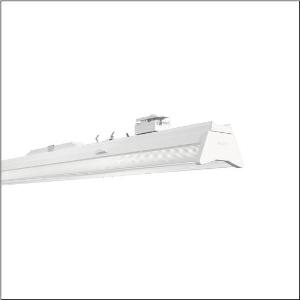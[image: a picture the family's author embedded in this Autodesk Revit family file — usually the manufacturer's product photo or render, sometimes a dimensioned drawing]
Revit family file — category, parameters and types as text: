
# Revit family: licross_r__11_performance_ho_51tm16dn4fxm_a8d0
name_source: partatom
category: Lighting Fixtures
units: mm (PartAtom-declared; Revit-internal decimal feet)

## family parameters
Cut with Voids When Loaded = No
Host = Face
Light Source = No
Part Type = Normal
Room Calculation Point = No
Round Connector Dimension = Use Diameter
Shared = No

## types (1)
- --- (1 x LED, 15460 lm, 87.3 W, 4000K)
    Apparent Load = 87 VA
    CIE Flux Codes = 63 87 95 78 100
    Color Rendering = 80
    Color Temperature = 4000K
    Default Elevation = 1800 mm
    Description = Licross® 11 Performance HO, luminaire insert, of sheet steel, galvanised, coil coated, white, length: 1.500mm, width: 120mm, height: 123mm, LED rated luminous flux: 15.460lm, light colour: 840, control gear: DALI 2, with plug, 5-pole, with phase selection, mains connection: 220..240V, AC, 50/60Hz, rated input power: 87W, halogen-free wiring, primary light control with lens, of plastic, primary optical cover: cover, of PMMA, light emission: direct/indirect distribution, primary light characteristic: symmetric, protection rating (complete): IP40, insulation class (complete): insulation class I (protective earthing), certification: CE, ENEC, VDE, UKCA, protection symbol: D if used in an environment without relevant dust loads with corresponding accessories, impact resistance: IK06, permissible ambient temperature for indoor applications: -25..+30°C, corresponds to IFS (International Featured Standards) requirements for safety and quality in the food industry, reducing of maximum allowable ambient temperature of 5°C with ceiling mounting, LABS conformity tested according to VDMA 24364:2018-05, packaging unit: 1 piece
    Height = 114 mm
    Lamp = 1 x LED
    Lamp Light Flux = 15460 lm
    Lamp Power = 87.3 W
    Lamp count = 1
    Length = 1500 mm
    Luminous efficacy = 177 lm/W
    Manufacturer = Siteco
    ModVariant = No
    Model = 51TM16DN4FXM
    Mounting Place = Ceiling
    Mounting Type = Pendant
    Number of Poles = 1
    OnlyDefault = Yes
    Power Factor = 1
    Product Name = Licross® 11 Performance HO
    Product group = luminaire insert
    ProductGroupID = 901
    Protection Class = Protection class I
    Protection Degree = IP 40
    RLX_Detail_Level = 1
    RLX_Emergency_Light_Flux = 0 lm
    RLX_Emergency_Type = 0
    RLX_Emergency_Type_DB = No
    RlxData = <blob elided: 34045 chars, md5=d069501e>
    Socket = socket
    Standby Power = 0 W
    System Light Flux = 15460 lm
    System Power = 87 W
    Type Comments = factory setting: luminous flux: 100 % | dim-lin: 254 | 589 mA
    Type Image = l_1256138.jpg
    URL = http://relux.com
    VarID = @adj_070281
    Voltage = 0 V
    Weight = 0.00 kg
    Width = 120 mm

## geometry (parser evidence)
native form markers: Blend x4, Sweep x10
no freeform markers — native parametric forms only
